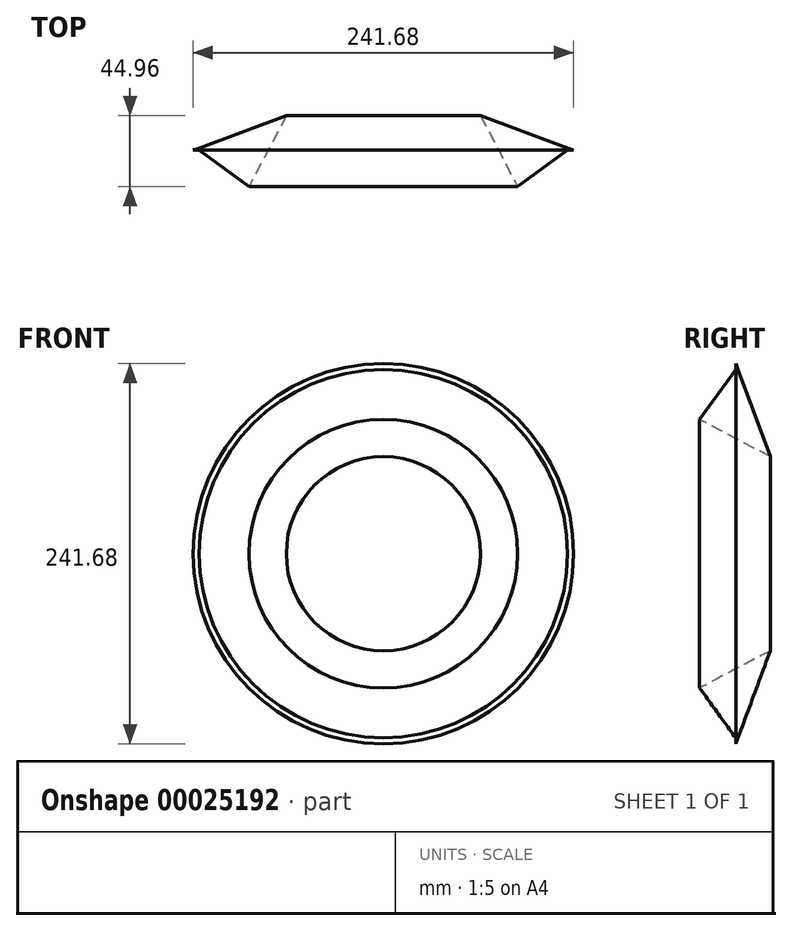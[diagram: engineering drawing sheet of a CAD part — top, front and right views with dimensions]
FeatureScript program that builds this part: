
annotation { "Feature Type Name" : "Feature", "Feature Type Description" : "" }
export const myFeature = defineFeature(function(context is Context, id is Id, definition is map)
    precondition{}
    {
        {
            var Q0;
            Q0=qCreatedBy(makeId("Top.planeOp"),FACE);
            var sketch = newSketch(context, id + "F0", { "sketchPlane" : qUnion([Q0])});
            skLineSegment(sketch, "E0", {"start": v(0, 0) * mm, "end": v(0, 51.9) * mm});
            skSolve(sketch);
        }
        {
            var Q0;
            Q0=qCreatedBy(makeId("Top.planeOp"),FACE);
            var sketch = newSketch(context, id + "F1", { "sketchPlane" : qUnion([Q0])});
            skLineSegment(sketch, "E1", {"start": v(85.29, 0) * mm, "end": v(61.63, 44.96) * mm});
            skLineSegment(sketch, "E2", {"start": v(61.63, 44.96) * mm, "end": v(116.87, 24.46) * mm});
            skLineSegment(sketch, "E3", {"start": v(116.96, 22.95) * mm, "end": v(85.29, 0) * mm});
            skLineSegment(sketch, "E4", {"start": v(116.87, 24.46) * mm, "end": v(120.84, 22.95) * mm});
            skLineSegment(sketch, "E5", {"start": v(120.84, 22.95) * mm, "end": v(116.96, 22.95) * mm});
            skSolve(sketch);
        }
        {
            var Q0;
            Q0=makeQuery(id+"F1.imprint","IMPRINT",FACE,{"disambiguationData":[TD([[makeQuery(id+"F1.imprint","IMPRINT",EDGE,{"derivedFrom":sQuery(id+"F1.wireOp",EDGE,"E1")}),-1.0]])]});
            var Q1;
            Q1=sQuery(id+"F0.wireOp",EDGE,"E0");
            revolve(context, id + "F2", {"entities" : qUnion([Q0]), "axis" : qUnion([Q1]), "revolveType" : RevolveType.FULL});
        }
    });
